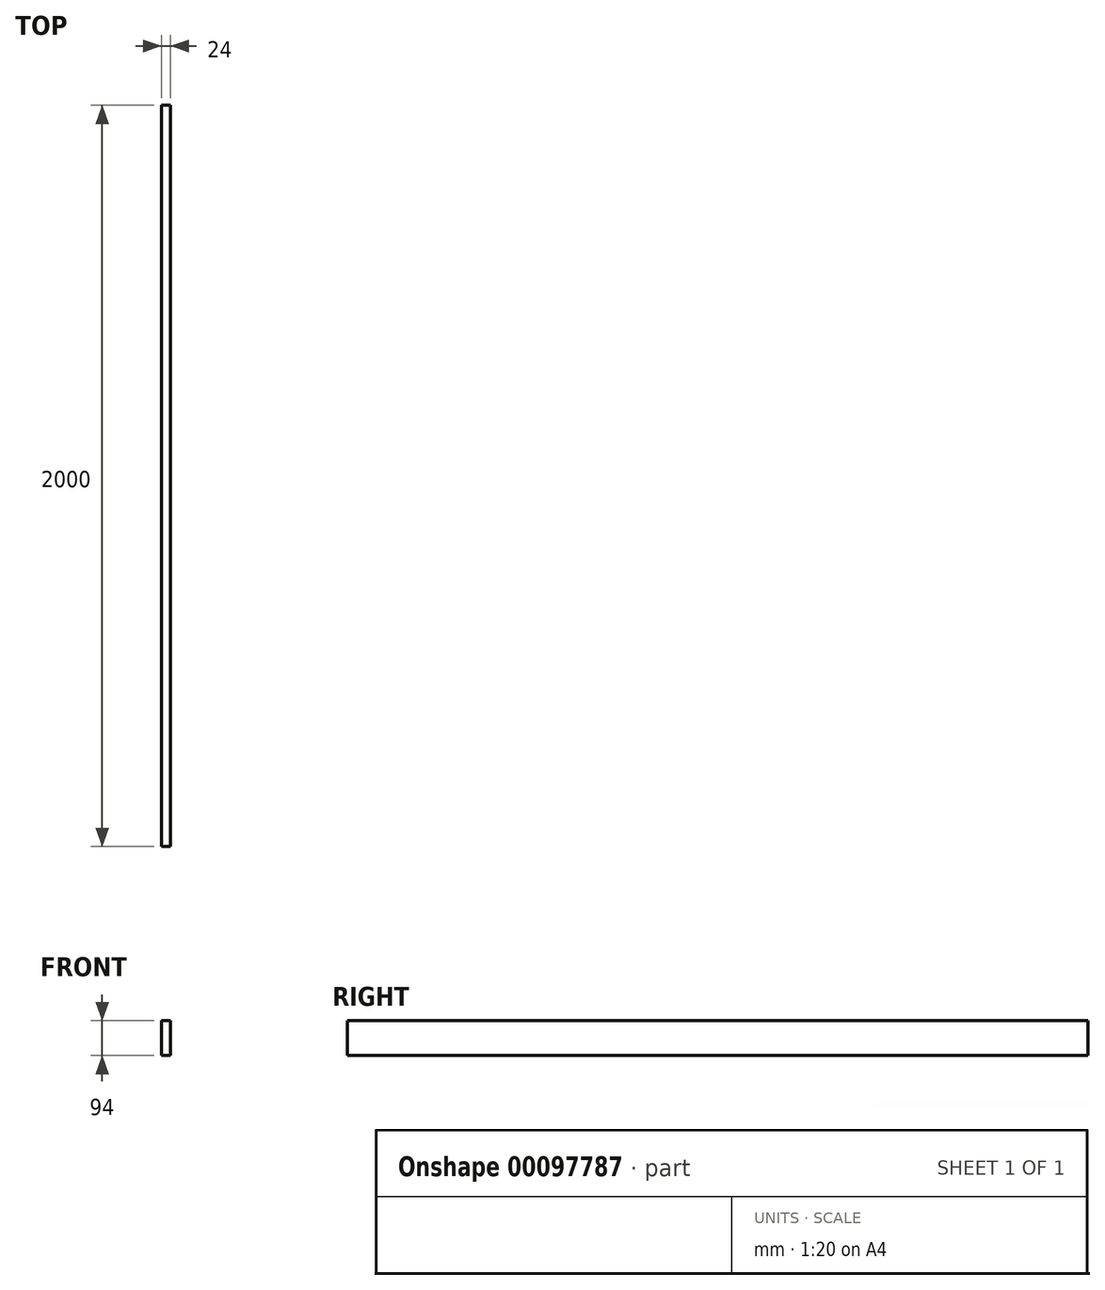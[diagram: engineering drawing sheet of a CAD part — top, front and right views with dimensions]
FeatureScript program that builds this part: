
annotation { "Feature Type Name" : "Feature", "Feature Type Description" : "" }
export const myFeature = defineFeature(function(context is Context, id is Id, definition is map)
    precondition{}
    {
        {
            var Q0;
            Q0=qCreatedBy(makeId("Front.planeOp"),FACE);
            var sketch = newSketch(context, id + "F0", { "sketchPlane" : qUnion([Q0])});
            skLineSegment(sketch, "E0.bottom", {"start": v(0, 0) * mm, "end": v(24, 0) * mm});
            skLineSegment(sketch, "E0.top", {"start": v(0, 94) * mm, "end": v(24, 94) * mm});
            skLineSegment(sketch, "E0.left", {"start": v(0, 0) * mm, "end": v(0, 94) * mm});
            skLineSegment(sketch, "E0.right", {"start": v(24, 0) * mm, "end": v(24, 94) * mm});
            skSolve(sketch);
        }
        {
            var Q0;
            Q0 = qSketchRegion(id + "F0", true);
            extrude(context, id + "F1", {"entities" : qUnion([Q0]), "oppositeDirection" : true, "depth" : 2000 * mm});
        }
    });
